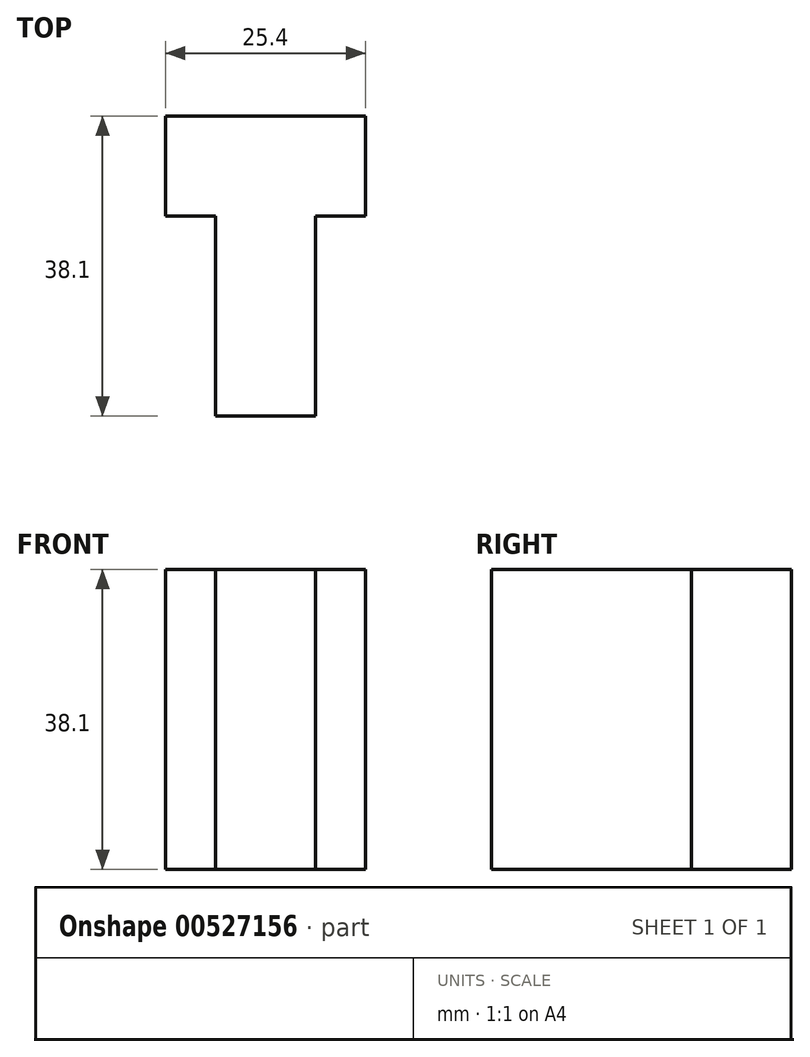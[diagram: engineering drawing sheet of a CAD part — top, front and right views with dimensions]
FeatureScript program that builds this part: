
annotation { "Feature Type Name" : "Feature", "Feature Type Description" : "" }
export const myFeature = defineFeature(function(context is Context, id is Id, definition is map)
    precondition{}
    {
        {
            var Q0;
            Q0=qCreatedBy(makeId("Top.planeOp"),FACE);
            var sketch = newSketch(context, id + "F0", { "sketchPlane" : qUnion([Q0])});
            skLineSegment(sketch, "E0", {"start": v(-13.2, 0) * mm, "end": v(-13.2, 25.4) * mm});
            skLineSegment(sketch, "E1", {"start": v(-13.2, 0) * mm, "end": v(-0.5, 0) * mm});
            skLineSegment(sketch, "E2", {"start": v(-0.5, 0) * mm, "end": v(-0.5, 25.4) * mm});
            skLineSegment(sketch, "E3", {"start": v(-13.2, 25.4) * mm, "end": v(-19.55, 25.4) * mm});
            skLineSegment(sketch, "E4", {"start": v(-19.55, 25.4) * mm, "end": v(-19.55, 38.1) * mm});
            skLineSegment(sketch, "E5", {"start": v(-19.55, 38.1) * mm, "end": v(5.85, 38.1) * mm});
            skLineSegment(sketch, "E6", {"start": v(5.85, 38.1) * mm, "end": v(5.85, 25.4) * mm});
            skLineSegment(sketch, "E7", {"start": v(5.85, 25.4) * mm, "end": v(-0.5, 25.4) * mm});
            skSolve(sketch);
        }
        {
            var Q0;
            Q0 = qSketchRegion(id + "F0", true);
            extrude(context, id + "F1", {"entities" : qUnion([Q0]), "depth" : 38.1 * mm, "offsetDistance" : 25.4 * mm});
        }
    });
